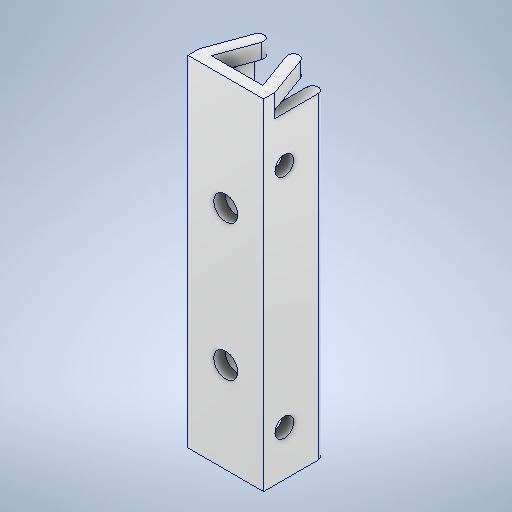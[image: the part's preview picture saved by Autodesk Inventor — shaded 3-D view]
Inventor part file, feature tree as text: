
AUTODESK INVENTOR PART (.ipt)
format: ipt  version: 2025 (Build 290162000, 162)  size: 348,672 bytes
history: native  units: mm
features: sketch x5, projected_geometry x4, extrude x3, hole x2, other x1, fillet x1
ambient origin geometry x8: Origin, YZ Plane, XZ Plane, XY Plane, X Axis, Y Axis, Z Axis, Center Point
bodies: Body1 (feature_tree)
feature tree (16):
  other  "Těleso1"
  extrude  "Vysunutí1"  Depth=1.5mm
  extrude  "Vysunutí2"  Depth=1.5mm
  extrude  "Vysunutí3"  Depth=1.5mm
  fillet  "Zaoblení1"  Radius=10.0mm
  hole  "Díra1"  [1 undecoded]
  hole  "Díra2"  [1 undecoded]
  sketch  "Náčrt1"
  sketch  "Náčrt2"
  projected_geometry  "Promítnutá smyčka1"
  sketch  "Náčrt3"
  projected_geometry  "Promítnutá smyčka2"
  sketch  "Náčrt4"
  projected_geometry  "Promítnutá smyčka3"
  sketch  "Náčrt5"
  projected_geometry  "Promítnutá smyčka4"
note: 2 required parameter values undecoded (feature->parameter linkage not recoverable at this tier; creation-order binding heuristic only, values carry confidence <= 0.55)
